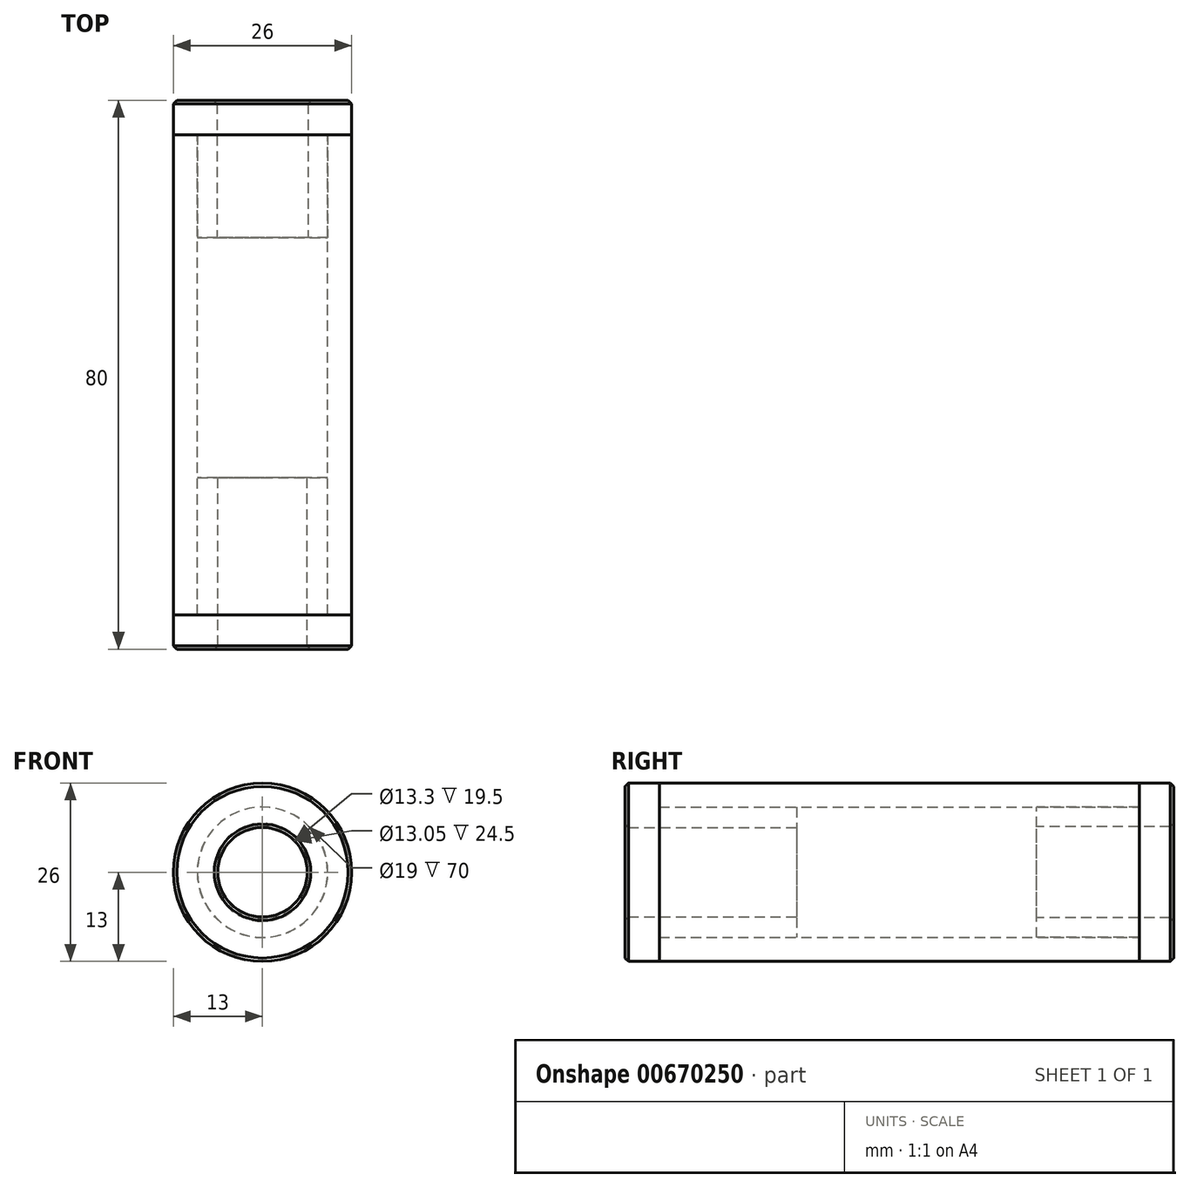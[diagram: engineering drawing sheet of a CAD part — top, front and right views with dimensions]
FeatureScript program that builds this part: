
annotation { "Feature Type Name" : "Feature", "Feature Type Description" : "" }
export const myFeature = defineFeature(function(context is Context, id is Id, definition is map)
    precondition{}
    {
        {
            var Q0;
            Q0=qCreatedBy(makeId("Front.planeOp"),FACE);
            var sketch = newSketch(context, id + "F0", { "sketchPlane" : qUnion([Q0])});
            skCircle(sketch, "E0", {"center": v(0, 0) * mm, "radius": 9.5 * mm});
            skCircle(sketch, "E1", {"center": v(0, 0) * mm, "radius": 13 * mm});
            skSolve(sketch);
        }
        {
            var Q0;
            Q0 = qSketchRegion(id + "F0", true);
            extrude(context, id + "F1", {"entities" : qUnion([Q0]), "endBound" : BoundingType.SYMMETRIC, "depth" : 70 * mm, "offsetDistance" : 25 * mm});
        }
        {
            var Q0;
            Q0=qCreatedBy(makeId("Right.planeOp"),FACE);
            var sketch = newSketch(context, id + "F2", { "sketchPlane" : qUnion([Q0])});
            skLineSegment(sketch, "E2.bottom", {"start": v(-15, 6.52) * mm, "end": v(-40, 6.52) * mm});
            skLineSegment(sketch, "E2.top", {"start": v(-15, 9.5) * mm, "end": v(-35, 9.5) * mm});
            skLineSegment(sketch, "E2.left", {"start": v(-15, 6.52) * mm, "end": v(-15, 9.5) * mm});
            skLineSegment(sketch, "E3", {"start": v(-40, 6.52) * mm, "end": v(-40, 13) * mm});
            skLineSegment(sketch, "E4", {"start": v(-40, 13) * mm, "end": v(-35, 13) * mm});
            skLineSegment(sketch, "E5", {"start": v(-35, 13) * mm, "end": v(-35, 9.5) * mm});
            skLineSegment(sketch, "E6", {"start": v(0, 0) * mm, "end": v(-46.69, 0) * mm});
            skSolve(sketch);
        }
        {
            var Q0;
            Q0=makeQuery(id+"F2.imprint","IMPRINT",FACE,{"disambiguationData":[TD([[makeQuery(id+"F2.imprint","IMPRINT",EDGE,{"derivedFrom":sQuery(id+"F2.wireOp",EDGE,"E2.bottom")}),-1.0]])]});
            var Q1;
            Q1=sQuery(id+"F2.wireOp",EDGE,"E6");
            revolve(context, id + "F3", {"entities" : qUnion([Q0]), "axis" : qUnion([Q1]), "revolveType" : RevolveType.FULL});
        }
        {
            var Q0;
            Q0=qCreatedBy(makeId("Right.planeOp"),FACE);
            var sketch = newSketch(context, id + "F4", { "sketchPlane" : qUnion([Q0])});
            skLineSegment(sketch, "E7.bottom", {"start": v(20, 9.5) * mm, "end": v(35, 9.5) * mm});
            skLineSegment(sketch, "E7.top", {"start": v(20, 6.65) * mm, "end": v(40, 6.65) * mm});
            skLineSegment(sketch, "E7.left", {"start": v(20, 9.5) * mm, "end": v(20, 6.65) * mm});
            skLineSegment(sketch, "E8", {"start": v(40, 6.65) * mm, "end": v(40, 13) * mm});
            skLineSegment(sketch, "E9", {"start": v(40, 13) * mm, "end": v(35, 13) * mm});
            skLineSegment(sketch, "E10", {"start": v(35, 13) * mm, "end": v(35, 9.5) * mm});
            skLineSegment(sketch, "E11", {"start": v(0, 0) * mm, "end": v(48.56, 0) * mm});
            skSolve(sketch);
        }
        {
            var Q0;
            Q0 = qSketchRegion(id + "F4", true);
            var Q1;
            Q1=sQuery(id+"F4.wireOp",EDGE,"E11");
            revolve(context, id + "F5", {"entities" : qUnion([Q0]), "axis" : qUnion([Q1]), "revolveType" : RevolveType.FULL});
        }
        {
            var Q0;
            Q0=makeQuery(id+"F5.opRevolve","SWEPT_FACE",FACE,{"disambiguationData":[OSD([sQuery(id+"F4.wireOp",EDGE,"E8")])]});
            var Q1;
            Q1=makeQuery(id+"F3.opRevolve","SWEPT_FACE",FACE,{"disambiguationData":[OSD([sQuery(id+"F2.wireOp",EDGE,"E3")])]});
            chamfer(context, id + "F6", {"entities" : qUnion([Q0, Q1]), "width" : 0.5 * mm, "tangentPropagation" : true});
        }
    });
